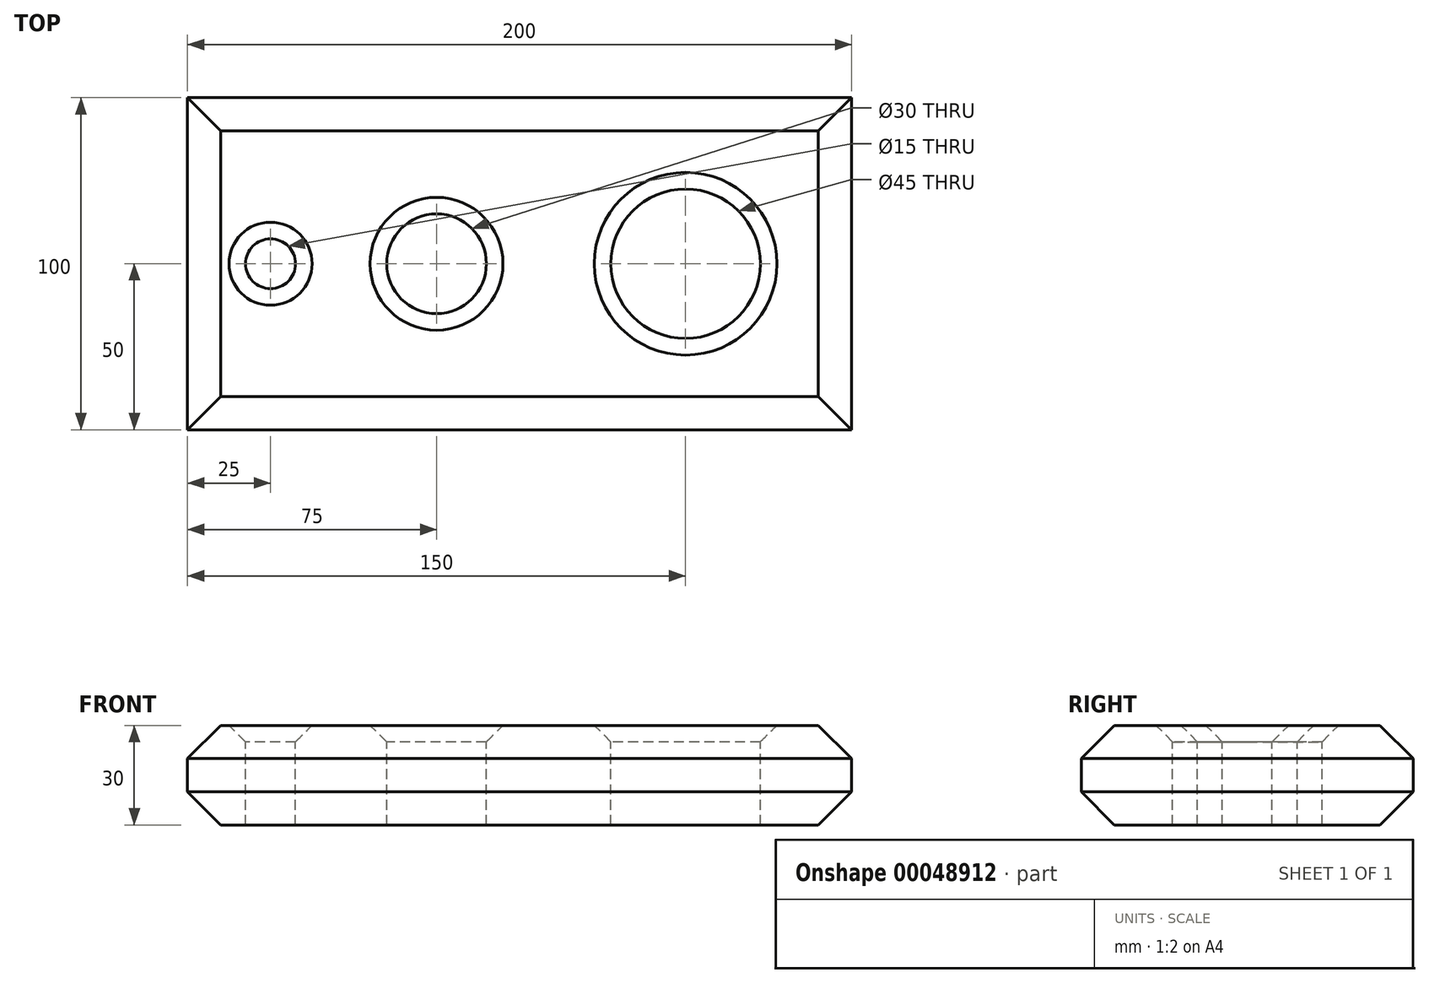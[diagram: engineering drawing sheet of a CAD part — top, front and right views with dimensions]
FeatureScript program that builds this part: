
annotation { "Feature Type Name" : "Feature", "Feature Type Description" : "" }
export const myFeature = defineFeature(function(context is Context, id is Id, definition is map)
    precondition{}
    {
        {
            var Q0;
            Q0=qCreatedBy(makeId("Top.planeOp"),FACE);
            var sketch = newSketch(context, id + "F0", { "sketchPlane" : qUnion([Q0])});
            skLineSegment(sketch, "E0.rect.bottom", {"start": v(100, 50) * mm, "end": v(-100, 50) * mm});
            skLineSegment(sketch, "E0.rect.top", {"start": v(100, -50) * mm, "end": v(-100, -50) * mm});
            skLineSegment(sketch, "E0.rect.left", {"start": v(100, 50) * mm, "end": v(100, -50) * mm});
            skLineSegment(sketch, "E0.rect.right", {"start": v(-100, 50) * mm, "end": v(-100, -50) * mm});
            skPoint(sketch, "E0.rect.middle", {"position": v(0, 0) * mm});
            skLineSegment(sketch, "E1", {"start": v(-100, 0) * mm, "end": v(-75, 0) * mm, "construction": true});
            skCircle(sketch, "E2", {"center": v(-75, 0) * mm, "radius": 7.5 * mm});
            skLineSegment(sketch, "E3", {"start": v(-75, 0) * mm, "end": v(-25, 0) * mm, "construction": true});
            skCircle(sketch, "E4", {"center": v(-25, 0) * mm, "radius": 15 * mm});
            skLineSegment(sketch, "E5", {"start": v(-25, 0) * mm, "end": v(50, 0) * mm, "construction": true});
            skCircle(sketch, "E6", {"center": v(50, 0) * mm, "radius": 22.5 * mm});
            skSolve(sketch);
        }
        {
            var Q0;
            Q0 = qSketchRegion(id + "F0", true);
            extrude(context, id + "F1", {"entities" : qUnion([Q0]), "oppositeDirection" : true, "depth" : 30 * mm});
        }
        {
            var Q0;
            Q0=makeQuery(id+"F1.opExtrude","CAP_EDGE",EDGE,{"disambiguationData":[OSD([sQuery(id+"F0.wireOp",EDGE,"E2")])],"isStart":true});
            var Q1;
            Q1=makeQuery(id+"F1.opExtrude","CAP_EDGE",EDGE,{"disambiguationData":[OSD([sQuery(id+"F0.wireOp",EDGE,"E4")])],"isStart":true});
            var Q2;
            Q2=makeQuery(id+"F1.opExtrude","CAP_EDGE",EDGE,{"disambiguationData":[OSD([sQuery(id+"F0.wireOp",EDGE,"E6")])],"isStart":true});
            chamfer(context, id + "F2", {"entities" : qUnion([Q0, Q1, Q2]), "chamferType" : ChamferType.OFFSET_ANGLE, "width" : 5 * mm, "oppositeDirection" : false, "angle" : 45 * degree, "tangentPropagation" : true});
        }
        {
            var Q0;
            Q0=makeQuery(id+"F1.opExtrude","CAP_EDGE",EDGE,{"disambiguationData":[OSD([sQuery(id+"F0.wireOp",EDGE,"E0.rect.top")])],"isStart":true});
            var Q1;
            Q1=makeQuery(id+"F1.opExtrude","CAP_EDGE",EDGE,{"disambiguationData":[OSD([sQuery(id+"F0.wireOp",EDGE,"E0.rect.left")])],"isStart":true});
            var Q2;
            Q2=makeQuery(id+"F1.opExtrude","CAP_EDGE",EDGE,{"disambiguationData":[OSD([sQuery(id+"F0.wireOp",EDGE,"E0.rect.left")])],"isStart":false});
            var Q3;
            Q3=makeQuery(id+"F1.opExtrude","CAP_EDGE",EDGE,{"disambiguationData":[OSD([sQuery(id+"F0.wireOp",EDGE,"E0.rect.top")])],"isStart":false});
            var Q4;
            Q4=makeQuery(id+"F1.opExtrude","CAP_EDGE",EDGE,{"disambiguationData":[OSD([sQuery(id+"F0.wireOp",EDGE,"E0.rect.bottom")])],"isStart":true});
            var Q5;
            Q5=makeQuery(id+"F1.opExtrude","CAP_EDGE",EDGE,{"disambiguationData":[OSD([sQuery(id+"F0.wireOp",EDGE,"E0.rect.bottom")])],"isStart":false});
            var Q6;
            Q6=makeQuery(id+"F1.opExtrude","CAP_EDGE",EDGE,{"disambiguationData":[OSD([sQuery(id+"F0.wireOp",EDGE,"E0.rect.right")])],"isStart":false});
            var Q7;
            Q7=makeQuery(id+"F1.opExtrude","CAP_EDGE",EDGE,{"disambiguationData":[OSD([sQuery(id+"F0.wireOp",EDGE,"E0.rect.right")])],"isStart":true});
            chamfer(context, id + "F3", {"entities" : qUnion([Q0, Q1, Q2, Q3, Q4, Q5, Q6, Q7]), "chamferType" : ChamferType.OFFSET_ANGLE, "width" : 10 * mm, "oppositeDirection" : false, "angle" : 45 * degree, "tangentPropagation" : true});
        }
    });
